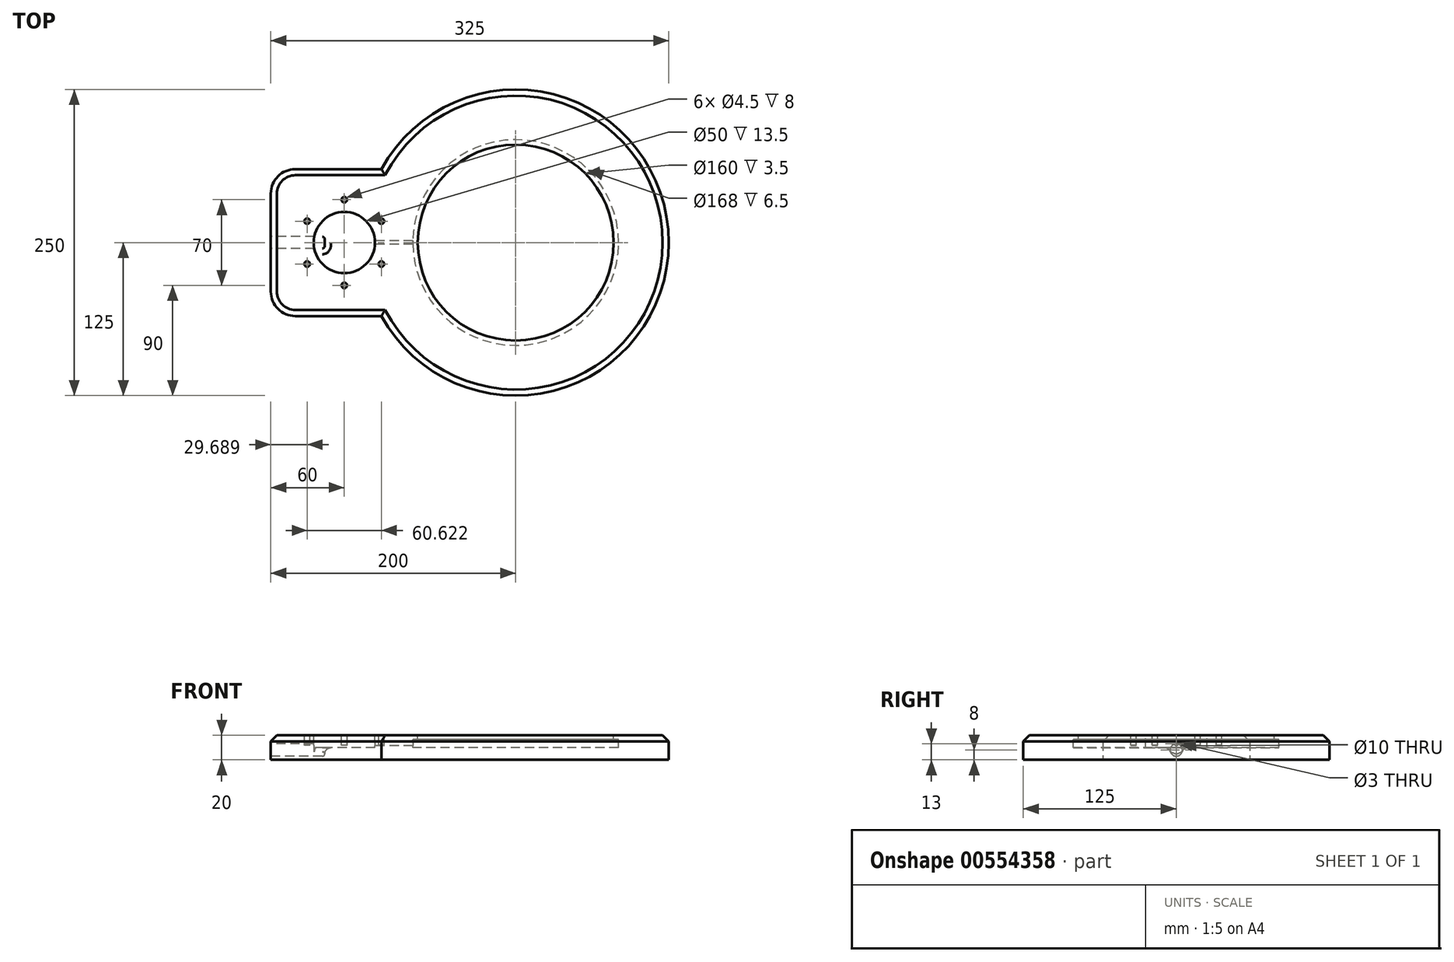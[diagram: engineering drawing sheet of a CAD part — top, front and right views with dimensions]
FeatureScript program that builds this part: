
annotation { "Feature Type Name" : "Feature", "Feature Type Description" : "" }
export const myFeature = defineFeature(function(context is Context, id is Id, definition is map)
    precondition{}
    {
        {
            var Q0;
            Q0=qCreatedBy(makeId("Top.planeOp"),FACE);
            var sketch = newSketch(context, id + "F0", { "sketchPlane" : qUnion([Q0])});
            skLineSegment(sketch, "E0.bottom", {"start": v(0, 0) * mm, "end": v(90.34, 0) * mm});
            skLineSegment(sketch, "E0.top", {"start": v(0, 120) * mm, "end": v(90.34, 120) * mm});
            skLineSegment(sketch, "E0.left", {"start": v(0, 0) * mm, "end": v(0, 120) * mm});
            skArc(sketch, "E1", {"start": v(90.34, 0) * mm, "mid": v(325, 60) * mm, "end": v(90.34, 120) * mm});
            skLineSegment(sketch, "E2", {"start": v(0, 0) * mm, "end": v(200, 0) * mm});
            skLineSegment(sketch, "E3", {"start": v(200, 0) * mm, "end": v(200, 60) * mm});
            skCircle(sketch, "E4", {"center": v(60, 60) * mm, "radius": 45 * mm, "construction": true});
            skLineSegment(sketch, "E5", {"start": v(60, 60) * mm, "end": v(0, 60) * mm});
            skLineSegment(sketch, "E6", {"start": v(200, 60) * mm, "end": v(0, 60) * mm, "construction": true});
            skLineSegment(sketch, "E7", {"start": v(60, 60) * mm, "end": v(60, 95) * mm, "construction": true});
            skCircle(sketch, "E8", {"center": v(60, 95) * mm, "radius": 2.5 * mm, "construction": true});
            skCircle(sketch, "E9.1.0", {"center": v(29.69, 77.5) * mm, "radius": 2.5 * mm, "construction": true});
            skCircle(sketch, "E9.2.0", {"center": v(29.69, 42.5) * mm, "radius": 2.5 * mm, "construction": true});
            skCircle(sketch, "E9.3.0", {"center": v(60, 25) * mm, "radius": 2.5 * mm, "construction": true});
            skCircle(sketch, "E9.4.0", {"center": v(90.31, 42.5) * mm, "radius": 2.5 * mm, "construction": true});
            skCircle(sketch, "E9.5.0", {"center": v(90.31, 77.5) * mm, "radius": 2.5 * mm, "construction": true});
            skSolve(sketch);
        }
        {
            var Q0;
            Q0 = qSketchRegion(id + "F0", true);
            extrude(context, id + "F1", {"entities" : qUnion([Q0]), "depth" : 20 * mm, "offsetDistance" : 25 * mm});
        }
        {
            var Q0;
            Q0=makeQuery(id+"F1.opExtrude","CAP_FACE",FACE,{"disambiguationData":[OSD([sQuery(id+"F0.wireOp",EDGE,"E0.top"),sQuery(id+"F0.wireOp",EDGE,"E0.left"),sQuery(id+"F0.wireOp",EDGE,"E1"),sQuery(id+"F0.wireOp",EDGE,"E2")])],"isStart":false});
            var sketch = newSketch(context, id + "F2", { "sketchPlane" : qUnion([Q0])});
            skLineSegment(sketch, "E10", {"start": v(0, 60) * mm, "end": v(60, 60) * mm, "construction": true});
            skLineSegment(sketch, "E11", {"start": v(60, 60) * mm, "end": v(60, 95) * mm, "construction": true});
            skCircle(sketch, "E12", {"center": v(60, 95) * mm, "radius": 2.25 * mm});
            skCircle(sketch, "E13.1.0", {"center": v(29.69, 77.5) * mm, "radius": 2.25 * mm});
            skCircle(sketch, "E13.2.0", {"center": v(29.69, 42.5) * mm, "radius": 2.25 * mm});
            skCircle(sketch, "E13.3.0", {"center": v(60, 25) * mm, "radius": 2.25 * mm});
            skCircle(sketch, "E13.4.0", {"center": v(90.31, 42.5) * mm, "radius": 2.25 * mm});
            skCircle(sketch, "E13.5.0", {"center": v(90.31, 77.5) * mm, "radius": 2.25 * mm});
            skPoint(sketch, "E13.center", {"position": v(60, 60) * mm});
            skSolve(sketch);
        }
        {
            var Q0;
            Q0 = qSketchRegion(id + "F2", true);
            extrude(context, id + "F3", {"entities" : qUnion([Q0]), "operationType" : NewBodyOperationType.REMOVE, "oppositeDirection" : true, "depth" : 8 * mm, "offsetDistance" : 25 * mm});
        }
        {
            var Q0;
            Q0=makeQuery(id+"F1.opExtrude","CAP_FACE",FACE,{"disambiguationData":[OSD([sQuery(id+"F0.wireOp",EDGE,"E0.top"),sQuery(id+"F0.wireOp",EDGE,"E0.left"),sQuery(id+"F0.wireOp",EDGE,"E1"),sQuery(id+"F0.wireOp",EDGE,"E2")])],"isStart":false});
            var sketch = newSketch(context, id + "F4", { "sketchPlane" : qUnion([Q0])});
            skCircle(sketch, "E14", {"center": v(200, 60) * mm, "radius": 80 * mm});
            skSolve(sketch);
        }
        {
            var Q0;
            Q0 = qSketchRegion(id + "F4", true);
            extrude(context, id + "F5", {"entities" : qUnion([Q0]), "operationType" : NewBodyOperationType.REMOVE, "oppositeDirection" : true, "depth" : 10 * mm, "offsetDistance" : 25 * mm});
        }
        {
            var Q0;
            Q0=makeQuery(id+"F1.opExtrude","CAP_FACE",FACE,{"disambiguationData":[OSD([sQuery(id+"F0.wireOp",EDGE,"E0.top"),sQuery(id+"F0.wireOp",EDGE,"E0.left"),sQuery(id+"F0.wireOp",EDGE,"E1"),sQuery(id+"F0.wireOp",EDGE,"E2")])],"isStart":false});
            var sketch = newSketch(context, id + "F6", { "sketchPlane" : qUnion([Q0])});
            skCircle(sketch, "E15", {"center": v(60, 60) * mm, "radius": 25 * mm});
            skLineSegment(sketch, "E16", {"start": v(0, 60) * mm, "end": v(60, 60) * mm, "construction": true});
            skSolve(sketch);
        }
        {
            var Q0;
            Q0 = qSketchRegion(id + "F6", true);
            extrude(context, id + "F7", {"entities" : qUnion([Q0]), "operationType" : NewBodyOperationType.REMOVE, "oppositeDirection" : true, "depth" : 10 * mm, "offsetDistance" : 25 * mm});
        }
        {
            var Q0;
            Q0=qCreatedBy(makeId("Right.planeOp"),FACE);
            var sketch = newSketch(context, id + "F8", { "sketchPlane" : qUnion([Q0])});
            skCircle(sketch, "E17", {"center": v(60, 8) * mm, "radius": 5 * mm});
            skLineSegment(sketch, "E18", {"start": v(0, 0) * mm, "end": v(60, 0) * mm, "construction": true});
            skLineSegment(sketch, "E19", {"start": v(60, 0) * mm, "end": v(60, 20) * mm, "construction": true});
            skPoint(sketch, "E20", {"position": v(60, 10) * mm});
            skSolve(sketch);
        }
        {
            var Q0;
            Q0=qCreatedBy(makeId("Right.planeOp"),FACE);
            cPlane(context, id + "F9", {"entities" : qUnion([Q0]), "cplaneType" : CPlaneType.OFFSET, "offset" : 63 * mm, "width" : 150 * mm, "height" : 150 * mm});
        }
        {
            var Q0;
            Q0 = qSketchRegion(id + "F8", true);
            extrude(context, id + "F10", {"entities" : qUnion([Q0]), "operationType" : NewBodyOperationType.REMOVE, "depth" : 44.1 * mm, "offsetDistance" : 25 * mm});
        }
        {
            var Q0;
            Q0=qCreatedBy(id+"F9.planeOp",FACE);
            var sketch = newSketch(context, id + "F11", { "sketchPlane" : qUnion([Q0])});
            skCircle(sketch, "E21", {"center": v(60, 13) * mm, "radius": 1.5 * mm});
            skLineSegment(sketch, "E22", {"start": v(60, 0) * mm, "end": v(0, 0) * mm, "construction": true});
            skLineSegment(sketch, "E23", {"start": v(60, 0) * mm, "end": v(60, 20) * mm, "construction": true});
            skSolve(sketch);
        }
        {
            var Q0;
            Q0 = qSketchRegion(id + "F11", true);
            extrude(context, id + "F12", {"entities" : qUnion([Q0]), "operationType" : NewBodyOperationType.REMOVE, "depth" : 60 * mm, "offsetDistance" : 25 * mm});
        }
        {
            var Q0;
            Q0=qCreatedBy(makeId("Front.planeOp"),FACE);
            cPlane(context, id + "F13", {"entities" : qUnion([Q0]), "cplaneType" : CPlaneType.OFFSET, "offset" : 60 * mm, "oppositeDirection" : true, "width" : 150 * mm, "height" : 150 * mm});
        }
        {
            var Q0;
            Q0=qCreatedBy(id+"F13.planeOp",FACE);
            var sketch = newSketch(context, id + "F14", { "sketchPlane" : qUnion([Q0])});
            skLineSegment(sketch, "E24.bottom", {"start": v(120, 16.5) * mm, "end": v(116, 16.5) * mm});
            skLineSegment(sketch, "E24.top", {"start": v(120, 10) * mm, "end": v(116, 10) * mm});
            skLineSegment(sketch, "E24.left", {"start": v(120, 16.5) * mm, "end": v(120, 10) * mm});
            skLineSegment(sketch, "E24.right", {"start": v(116, 16.5) * mm, "end": v(116, 10) * mm});
            skLineSegment(sketch, "E25", {"start": v(200, 0) * mm, "end": v(200, 16.64) * mm});
            skSolve(sketch);
        }
        {
            var Q0;
            Q0 = qSketchRegion(id + "F14", true);
            var Q1;
            Q1=sQuery(id+"F14.wireOp",EDGE,"E25");
            revolve(context, id + "F15", {"operationType" : NewBodyOperationType.REMOVE, "entities" : qUnion([Q0]), "axis" : qUnion([Q1]), "revolveType" : RevolveType.FULL, "oppositeDirection" : true});
        }
        {
            var Q0;
            Q0=makeQuery(id+"F10.boolean.opBoolean","COPY",EDGE,{"derivedFrom":makeQuery(id+"F10.opExtrude","CAP_EDGE",EDGE,{"disambiguationData":[OSD([sQuery(id+"F8.wireOp",EDGE,"E17")])],"isStart":false})});
            fillet(context, id + "F16", {"entities" : qUnion([Q0]), "radius" : 2 * mm, "tangentPropagation" : true, "allowEdgeOverflow" : false});
        }
        {
            var Q0;
            Q0=makeQuery(id+"F10.boolean.opBoolean","INTERSECT",EDGE,{"derivedFrom":[makeQuery(id+"F7.boolean.opBoolean","COPY",FACE,{"derivedFrom":makeQuery(id+"F7.opExtrude","CAP_FACE",FACE,{"disambiguationData":[OSD([sQuery(id+"F6.wireOp",EDGE,"E15")])],"isStart":false})}),makeQuery(id+"F10.opExtrude","CAP_FACE",FACE,{"disambiguationData":[OSD([sQuery(id+"F8.wireOp",EDGE,"E17")])],"isStart":false})]});
            fillet(context, id + "F17", {"entities" : qUnion([Q0]), "radius" : 5 * mm, "tangentPropagation" : true, "allowEdgeOverflow" : false});
        }
        {
            var Q0;
            Q0=makeQuery(id+"F1.opExtrude","SWEPT_EDGE",EDGE,{"disambiguationData":[OSD([sQuery(id+"F0.wireOp",EDGE,"E0.top"),sQuery(id+"F0.wireOp",EDGE,"E0.left")])]});
            var Q1;
            Q1=makeQuery(id+"F1.opExtrude","SWEPT_EDGE",EDGE,{"disambiguationData":[OSD([sQuery(id+"F0.wireOp",EDGE,"E0.left"),sQuery(id+"F0.wireOp",EDGE,"E2")])]});
            fillet(context, id + "F18", {"entities" : qUnion([Q0, Q1]), "radius" : 20 * mm, "tangentPropagation" : true, "allowEdgeOverflow" : false});
        }
        {
            var Q0;
            Q0=makeQuery(id+"F1.opExtrude","CAP_EDGE",EDGE,{"disambiguationData":[OSD([sQuery(id+"F0.wireOp",EDGE,"E0.bottom")])],"isStart":false});
            var Q1;
            Q1=makeQuery(id+"F1.opExtrude","CAP_EDGE",EDGE,{"disambiguationData":[OSD([sQuery(id+"F0.wireOp",EDGE,"E0.left")])],"isStart":false});
            var Q2;
            Q2=makeQuery(id+"F1.opExtrude","CAP_EDGE",EDGE,{"disambiguationData":[OSD([sQuery(id+"F0.wireOp",EDGE,"E0.right")])],"isStart":false});
            var Q3;
            Q3=makeQuery(id+"F1.opExtrude","CAP_EDGE",EDGE,{"disambiguationData":[OSD([sQuery(id+"F0.wireOp",EDGE,"E0.top")])],"isStart":false});
            var Q4;
            Q4=makeQuery(id+"F1.opExtrude","CAP_EDGE",EDGE,{"disambiguationData":[OSD([sQuery(id+"F0.wireOp",EDGE,"E1")])],"isStart":false});
            var Q5;
            Q5=makeQuery(id+"F1.opExtrude","CAP_EDGE",EDGE,{"disambiguationData":[OSD([sQuery(id+"F0.wireOp",EDGE,"E2")])],"isStart":false});
            chamfer(context, id + "F19", {"entities" : qUnion([Q0, Q1, Q2, Q3, Q4, Q5]), "width" : 5 * mm, "tangentPropagation" : true});
        }
    });
